# Revit family: NBS_Senator_MeetingPods_TeamSpace_PDTS18
name_source: partatom
category: Furniture
revit_build: Autodesk Revit 2018 (Build: 20190510_1515(x64)
units: mm (PartAtom-declared; Revit-internal decimal feet)

## family parameters
Always vertical = Yes
Cut with Voids When Loaded = No
Room Calculation Point = No
Shared = No
Work Plane-Based = No

## types (1)
- PDTS18
    Accessories = Monitor arms, PU desk accessories, desk top accessories, CPU holders, electrical accessories, coat hanger, name plate, A2 dry wipe board with hanger, A3 dry wipe board with hanger
    AssetType = Fixed
    BIMObjectName = NBS_Senator_MeetingPods_TeamSpace_PDTS18
    Category = Pr_40_50_12_53: Meeting pods
    Description = Double meeting space optimises interior space
    DurationUnit = year
    ExpectedLife = 10
    FabricFinishOptions = Plymouth, fairfield, latymer, lancaster, silcoates, silverdale, st andrews, trevelyan, ulster, wellington, wesley, manchester,
    Features = Internal frame with multi-layered acoustic foam, levelling adjusters, blazer fabric, outer vertical panels
    Finish = Outer vertical panels upholstered in camira, blazer fabric Two tone is standard
    FinishOptions = Carini walnut, mocha, autumn, strata oak, maple, highland oak, beech, winter oak, hacienda white, white, light grey, denim, clay, lemon sorbet
    FramesColour = Black, white
    IfcExportAs = IfcFurnitureType
    IfcExportType = USERDEFINED
    IsBuiltIn = No
    ManufacturerName = The Senator Group
    ManufacturerURL = www.senator.co.uk
    Material = Fabric, metal, plastic
    MiddlePanelMaterial = NBS_Senator_White
    ModelNumber = PDTS18
    ModelReference = Pods-TeamSpace_PDTS18
    NBSCertification = www.nationalbimlibrary.com/cert/pp5ag0gz
    NBSDescription = Meeting pods
    NBSReference = 45-35-20/342
    Name = MeetingPods_TeamSpace_PDTS18_Senator
    NominalDepth = 2500 mm  [stored 8.2021 ft]
    NominalHeight = 1800 mm  [stored 5.90551 ft]
    NominalLength = 4950 mm  [stored 16.2402 ft]
    NominalWidth = 4950 mm  [stored 16.2402 ft]
    PanelWidth = 50 mm  [stored 0.164042 ft]
    PodDepth = 2500 mm  [stored 8.2021 ft]
    PodHeight = 1800 mm  [stored 5.90551 ft]
    PodWidth = 4950 mm  [stored 16.2402 ft]
    Size = 2500 x 1800 x 4950 mm
    Status = UNSET
    Style = Pods
    SustainabilityPerformance = 99% recyclable
    Uniclass2015Code = Meeting pods
    Uniclass2015Title = Pr_40_50_12_53
    Uniclass2015Version = Products v1.16
    Version = 1
    WallPanelAMaterial = NBS_Senator_StAndrews
    WallPanelBMaterial = NBS_Senator_White
    WarrantyDescription = Senator warrants that its manufactured products are free from manufacturing defects - in materials or workmanship - for a period of ten (10) years on Senator Seating ranges; and fifteen (15) years on Senator Desking ranges - exceptions are listed below. Senator will repair or replace (at Senator’s sole discretion) with comparable free of charge materials / components, any product / component, which fails under normal use in a single shift environment, as a result of a defect in the materials and / or workmanship
    WarrantyDurationParts = 10
    WarrantyDurationUnit = year

note: [stored X ft] marks values corroborated as IEEE doubles in the binary element streams (Revit-internal decimal feet)

## geometry (parser evidence)
native form markers: Sweep x2
no freeform markers — native parametric forms only
